# Revit family: FRC25
name_source: partatom
category: Generic Models
revit_build: Autodesk Revit LT 2017 (Build: 20160225_1515(x64)
units: mm (PartAtom-declared; Revit-internal decimal feet)

## family parameters
Always vertical = No
Can host rebar = No
Cut with Voids When Loaded = No
Part Type = Normal
Room Calculation Point = No
Round Connector Dimension = Use Diameter
Shared = No
Work Plane-Based = Yes

## types (1)
- NBS Standard Parameters
    BIMObjectName = Metpro_metprolibrary_Steelclips_cableclips_firerestant
    Default Elevation = 1219 mm
    Description = FRC25 - Fire Resistant Clip
    DurationUnit = year
    Finish = Pre Galvanised
    Keynote = Fully Compliant to Amendment 3 BS7671
    ManufacturerName = Metpro Ltd
    ManufacturerURL = www.metpro.co.uk
    Material = Steel
    ModelReference = FRC25
    NBSDescription = Steel Clips
    NBSReference = 45-50-17/410
    NominalHeight = 24 mm  [stored 0.0787402 ft]
    NominalLength = 20 mm  [stored 0.0656168 ft]
    NominalWidth = 20 mm  [stored 0.0656168 ft]
    ProductInformation = www.metpro.co.uk/pdf/frc25.pdf
    Size = 25mm
    Uniclass2 = Pr_20_29_14_86
    Version = 1
    WarrantyDurationUnit = 1 year
    Weight = 0.004Kg

note: [stored X ft] marks values corroborated as IEEE doubles in the binary element streams (Revit-internal decimal feet)

## geometry (parser evidence)
native form markers: Sweep x2
no freeform markers — native parametric forms only
